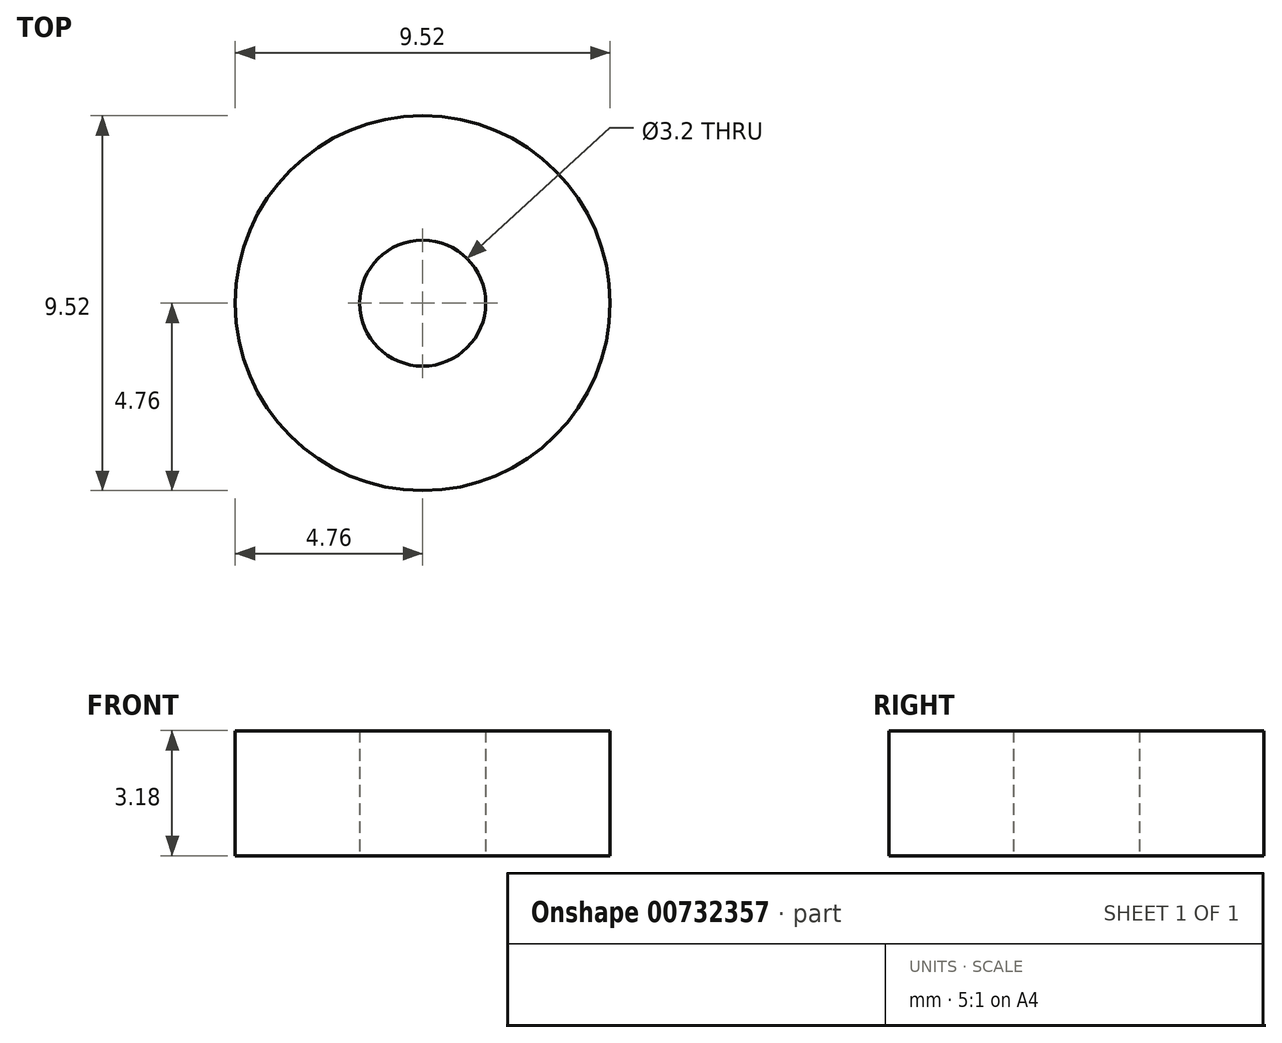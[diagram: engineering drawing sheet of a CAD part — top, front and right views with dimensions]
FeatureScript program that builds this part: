
annotation { "Feature Type Name" : "Feature", "Feature Type Description" : "" }
export const myFeature = defineFeature(function(context is Context, id is Id, definition is map)
    precondition{}
    {
        {
            var Q0;
            Q0=qCreatedBy(makeId("Top.planeOp"),FACE);
            var sketch = newSketch(context, id + "F0", { "sketchPlane" : qUnion([Q0])});
            skCircle(sketch, "E0", {"center": v(0, 0) * mm, "radius": 4.76 * mm});
            skCircle(sketch, "E1", {"center": v(0, 0) * mm, "radius": 1.6 * mm});
            skSolve(sketch);
        }
        {
            var Q0;
            Q0=makeQuery(id+"F0.imprint","IMPRINT",FACE,{"disambiguationData":[TD([[makeQuery(id+"F0.imprint","IMPRINT",EDGE,{"derivedFrom":sQuery(id+"F0.wireOp",EDGE,"E0")}),1.0]])]});
            extrude(context, id + "F1", {"entities" : qUnion([Q0]), "depth" : 3.17 * mm, "offsetDistance" : 25.4 * mm});
        }
    });
